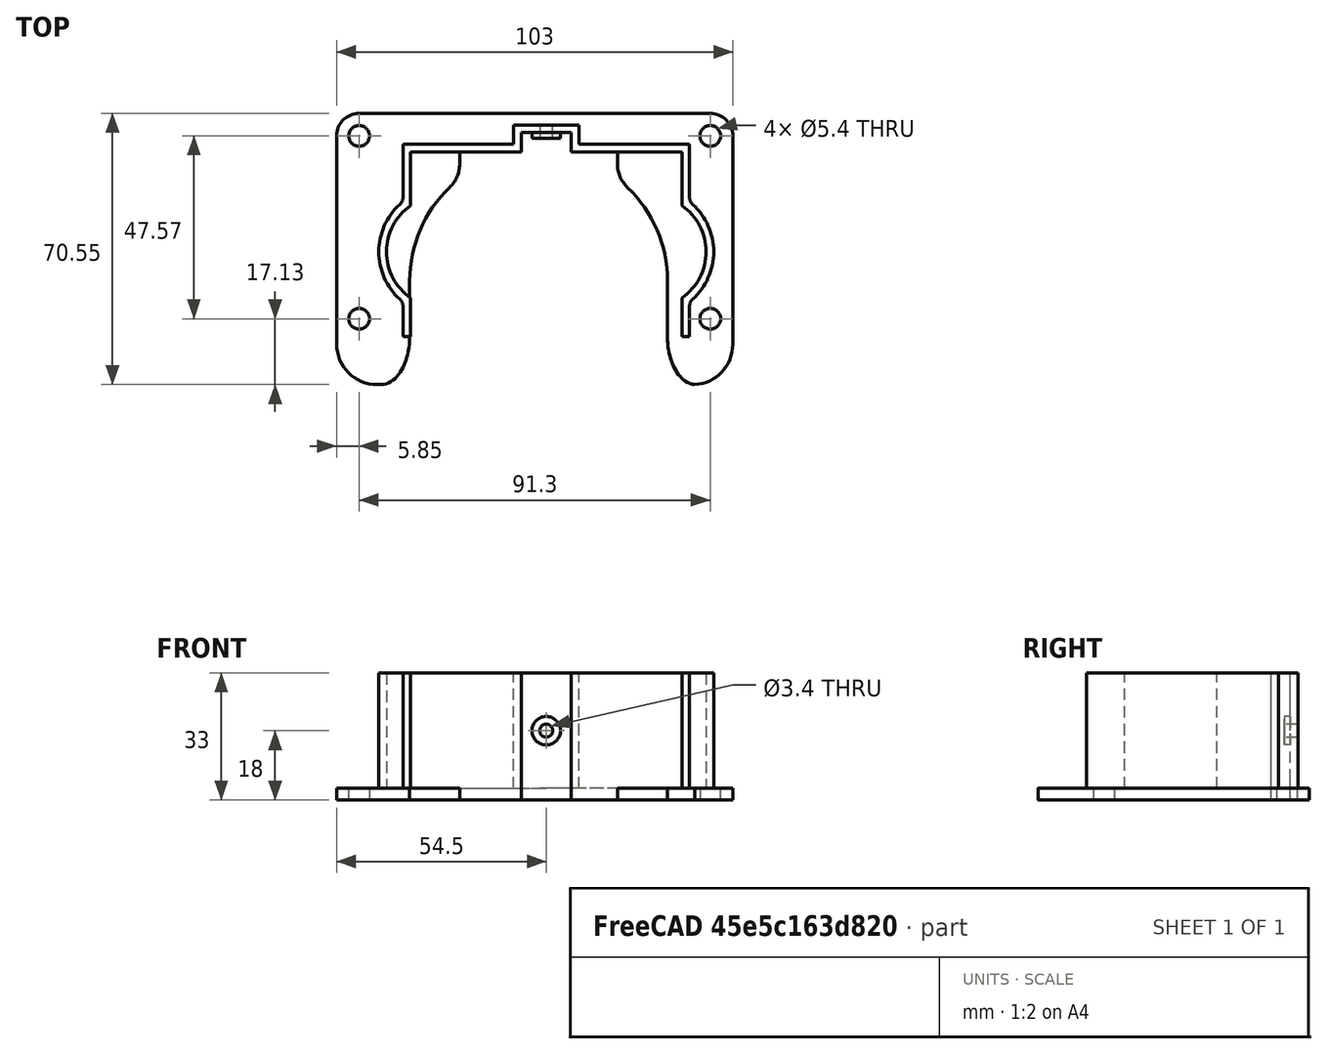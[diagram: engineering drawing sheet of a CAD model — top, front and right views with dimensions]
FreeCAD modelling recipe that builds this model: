
FCSTD DOCUMENT  (FreeCAD 0.19R24366 (Git))
Label: Направляющая датёра
License: All rights reserved
LicenseURL: http://en.wikipedia.org/wiki/All_rights_reserved
objects: Sketcher::SketchObject×6, PartDesign::Pad×3, PartDesign::Pocket×3, PartDesign::Mirrored×3, Mesh::Feature×1, PartDesign::Body×1
note: 22 computed .brp shape members not serialized (recipe doc carries the construction recipe); baked Part::Feature solids carry a one-line shape summary decoded from their .brp

FEATURE [Mesh::Feature] _____________________________________7  label="Направляющая датёра7"
FEATURE [Sketcher::SketchObject] Sketch
  FullyConstrained = true
  MapMode = 5
  Support = -> [XY_Plane]
  sketch-geometry (8):
    g0: Circle CenterX=45.65 CenterY=30.15 CenterZ=0 NormalX=0 NormalY=0 NormalZ=1 AngleXU=0 Radius=2.7
    g1: Circle CenterX=45.65 CenterY=-17.42 CenterZ=0 NormalX=0 NormalY=0 NormalZ=1 AngleXU=0 Radius=2.7
    g2: ArcOfCircle CenterX=45.65 CenterY=30.15 CenterZ=0 NormalX=0 NormalY=0 NormalZ=1 AngleXU=0 Radius=5.85 StartAngle=6.28319 EndAngle=7.85398
    g3: ArcOfCircle CenterX=41 CenterY=-24.05 CenterZ=0 NormalX=0 NormalY=0 NormalZ=1 AngleXU=0 Radius=10.5 StartAngle=4.71239 EndAngle=6.28319
    g4: LineSegment StartX=45.65 StartY=36 StartZ=0 EndX=0 EndY=36 EndZ=0
    g5: LineSegment StartX=0 StartY=36 StartZ=0 EndX=0 EndY=-34.55 EndZ=0
    g6: LineSegment StartX=0 StartY=-34.55 StartZ=0 EndX=41 EndY=-34.55 EndZ=0
    g7: LineSegment StartX=51.5 StartY=-24.05 StartZ=0 EndX=51.5 EndY=30.15 EndZ=0
  constraints (25):
    c: Coincident(g2,g0)
    c: Coincident(g4,g2)
    c: PointOnObject(g4,g-2)
    c: Horizontal(g4)
    c: Coincident(g5,g4)
    c: PointOnObject(g5,g-2)
    c: Coincident(g6,g5)
    c: Coincident(g6,g3)
    c: Coincident(g7,g3)
    c: Coincident(g7,g2)
    c: Vertical(g7)
    c: Horizontal(g6)
    c: Diameter(g0) = 5.4
    c: Vertical(g1,g0)
    c: Equal(g1,g0)
    c: DistanceX(g0) = 45.65
    c: DistanceY(g0) = 30.15
    c: DistanceY(g1) = -17.42
    c: Diameter(g2) = 11.7
    c: Tangent(g2,g4)
    c: Tangent(g2,g7)
    c: Tangent(g3,g7)
    c: Tangent(g6,g3)
    c: Diameter(g3) = 21
    c: DistanceY(g5) = -34.55
FEATURE [Sketcher::SketchObject] Sketch001
  AttachmentOffset = pos=(1,0,0) rot=(0,0,1;0rad)
  FullyConstrained = true
  MapMode = 5
  Placement = pos=(1,0,0) rot=(0,0,1;0rad)
  Support = -> [XY_Plane]
  sketch-geometry (12):
    g0: LineSegment StartX=20.5 StartY=22.8809 StartZ=0 EndX=20.5 EndY=26 EndZ=0
    g1: LineSegment StartX=20.5 StartY=26 StartZ=0 EndX=0 EndY=26 EndZ=0
    g2: ArcOfCircle CenterX=29 CenterY=22.8809 CenterZ=0 NormalX=0 NormalY=0 NormalZ=1 AngleXU=0 Radius=8.5 StartAngle=3.14159 EndAngle=3.95024
    g3: ArcOfCircle CenterX=0 CenterY=-7.5 CenterZ=0 NormalX=0 NormalY=0 NormalZ=1 AngleXU=0 Radius=33.5 StartAngle=8.26042e-09 EndAngle=0.808649
    g4: LineSegment StartX=41 StartY=-34.55 StartZ=0 EndX=0 EndY=-34.55 EndZ=0
    g5: LineSegment StartX=0 StartY=-34.55 StartZ=0 EndX=0 EndY=26 EndZ=0
    g6: LineSegment StartX=33.5 StartY=-7.5 StartZ=0 EndX=33.5 EndY=-22 EndZ=0
    g7: ArcOfEllipse CenterX=41 CenterY=-22 CenterZ=0 NormalX=0 NormalY=0 NormalZ=1 MajorRadius=12.55 MinorRadius=7.5 AngleXU=1.5708 StartAngle=1.5708 EndAngle=3.14159
    g8: LineSegment StartX=41 StartY=-9.45 StartZ=0 EndX=41 EndY=-34.55 EndZ=0
    g9: LineSegment StartX=33.5 StartY=-22 StartZ=0 EndX=48.5 EndY=-22 EndZ=0
    g10: GeomPoint X=41 Y=-11.9376 Z=0
    g11: GeomPoint X=41 Y=-32.0624 Z=0
  constraints (30):
    c: Vertical(g0)
    c: Coincident(g1,g0)
    c: PointOnObject(g1,g-2)
    c: Horizontal(g1)
    c: Coincident(g2,g0)
    c: PointOnObject(g3,g-2)
    c: Coincident(g3,g2)
    c: PointOnObject(g4,g-2)
    c: Horizontal(g4)
    c: Coincident(g5,g4)
    c: Coincident(g5,g1)
    c: DistanceY(g4) = -34.55
    c: Coincident(g6,g3)
    c: Vertical(g6)
    c: Diameter(g3) = 67
    c: DistanceY(g1) = 26
    c: DistanceX(g0) = 20.5
    c: PointOnObject(g1,g3)
    c: Tangent(g3,g2)
    c: Tangent(g2,g0)
    c: Diameter(g2) = 17
    c: Tangent(g6,g3)
    c: InternalAlignment(g8-g11 -> g7) x4
    c: Coincident(g7,g4)
    c: Coincident(g7,g6)
    c: Vertical(g8)
    c: Tangent(g7,g6)
    c: Tangent(g7,g4)
    c: DistanceY(g6) = -22
    c: DistanceX(g4) = 41
FEATURE [Sketcher::SketchObject] Sketch002
  AttachmentOffset = pos=(3,0,3) rot=(0,0,1;0rad)
  FullyConstrained = true
  MapMode = 5
  Placement = pos=(3,0,3) rot=(0,0,1;0rad)
  Support = -> [XY_Plane]
  expr: Constraints[60] = Sketch001.Constraints[14]
  expr: Constraints[62] = Sketch001.Constraints[16]
  expr: Constraints[61] = Sketch001.Constraints[15]
  expr: Constraints[66] = Sketch001.Constraints[20]
  expr: Constraints[57] = Sketch001.Constraints[11]
  expr: Constraints[77] = Sketch001.Constraints[31]
  expr: Constraints[78] = Sketch001.Constraints[32]
  sketch-geometry (31):
    g0: LineSegment StartX=35.25 StartY=-22 StartZ=0 EndX=37.25 EndY=-22 EndZ=0
    g1: LineSegment StartX=35.25 StartY=-22 StartZ=0 EndX=35.25 EndY=-12 EndZ=0
    g2: LineSegment StartX=35.25 StartY=12 StartZ=0 EndX=35.25 EndY=26 EndZ=0
    g3: LineSegment StartX=35.25 StartY=26 StartZ=0 EndX=6.5 EndY=26 EndZ=0
    g4: LineSegment StartX=6.5 StartY=26 StartZ=0 EndX=6.5 EndY=31 EndZ=0
    g5: LineSegment StartX=6.5 StartY=31 StartZ=0 EndX=0 EndY=31 EndZ=0
    g6: LineSegment StartX=37.25 StartY=-22 StartZ=0 EndX=37.25 EndY=-14.1617 EndZ=0
    g7: LineSegment StartX=37.25 StartY=14.1617 StartZ=0 EndX=37.25 EndY=28 EndZ=0
    g8: LineSegment StartX=37.25 StartY=28 StartZ=0 EndX=8.5 EndY=28 EndZ=0
    g9: LineSegment StartX=8.5 StartY=28 StartZ=0 EndX=8.5 EndY=33 EndZ=0
    g10: LineSegment StartX=8.5 StartY=33 StartZ=0 EndX=0 EndY=33 EndZ=0
    g11: ArcOfCircle CenterX=26.9338 CenterY=1.9e-15 CenterZ=0 NormalX=0 NormalY=0 NormalZ=1 AngleXU=0 Radius=14.6 StartAngle=5.31842 EndAngle=7.24796
    g12: ArcOfCircle CenterX=26.9338 CenterY=1.9e-15 CenterZ=0 NormalX=0 NormalY=0 NormalZ=1 AngleXU=0 Radius=16.6 StartAngle=5.44796 EndAngle=7.11842
    g13: ArcOfCircle CenterX=39.75 CenterY=14.1617 CenterZ=0 NormalX=0 NormalY=0 NormalZ=1 AngleXU=0 Radius=2.5 StartAngle=3.14159 EndAngle=3.97682
    g14: ArcOfCircle CenterX=39.75 CenterY=-14.1617 CenterZ=0 NormalX=0 NormalY=0 NormalZ=1 AngleXU=0 Radius=2.5 StartAngle=2.30636 EndAngle=3.14159
    g15: LineSegment StartX=35.25 StartY=26 StartZ=0 EndX=37.25 EndY=26 EndZ=0
    g16: LineSegment StartX=8.5 StartY=28 StartZ=0 EndX=8.5 EndY=26 EndZ=0
    g17: LineSegment StartX=0 StartY=33 StartZ=0 EndX=0 EndY=31 EndZ=0
    g18: LineSegment StartX=20.5 StartY=22.8809 StartZ=0 EndX=20.5 EndY=26 EndZ=0
    g19: LineSegment StartX=20.5 StartY=26 StartZ=0 EndX=0 EndY=26 EndZ=0
    g20: ArcOfCircle CenterX=29 CenterY=22.8809 CenterZ=0 NormalX=0 NormalY=0 NormalZ=1 AngleXU=0 Radius=8.5 StartAngle=3.14159 EndAngle=3.95024
    g21: ArcOfCircle CenterX=0 CenterY=-7.5 CenterZ=0 NormalX=0 NormalY=0 NormalZ=1 AngleXU=0 Radius=33.5 StartAngle=6.28319 EndAngle=7.09183
    g22: LineSegment StartX=41 StartY=-34.55 StartZ=0 EndX=0 EndY=-34.55 EndZ=0
    g23: LineSegment StartX=0 StartY=-34.55 StartZ=0 EndX=0 EndY=26 EndZ=0
    g24: LineSegment StartX=33.5 StartY=-7.5 StartZ=0 EndX=33.5 EndY=-22 EndZ=0
    g25: ArcOfEllipse CenterX=41 CenterY=-22 CenterZ=0 NormalX=0 NormalY=0 NormalZ=1 MajorRadius=12.55 MinorRadius=7.5 AngleXU=1.5708 StartAngle=1.5708 EndAngle=3.14159
    g26: LineSegment StartX=41 StartY=-9.45 StartZ=0 EndX=41 EndY=-34.55 EndZ=0
    g27: LineSegment StartX=33.5 StartY=-22 StartZ=0 EndX=48.5 EndY=-22 EndZ=0
    g28: GeomPoint X=41 Y=-11.9376 Z=0
    g29: GeomPoint X=41 Y=-32.0624 Z=0
    g30: LineSegment StartX=8.5 StartY=28 StartZ=0 EndX=6.5 EndY=28 EndZ=0
  constraints (89):
    c: Horizontal(g0)
    c: Coincident(g1,g0)
    c: Vertical(g1)
    c: Vertical(g2)
    c: Coincident(g3,g2)
    c: Horizontal(g3)
    c: Coincident(g4,g3)
    c: Vertical(g4)
    c: Coincident(g5,g4)
    c: Horizontal(g5)
    c: Coincident(g6,g0)
    c: Vertical(g6)
    c: Vertical(g7)
    c: Coincident(g8,g7)
    c: Horizontal(g8)
    c: Coincident(g9,g8)
    c: Vertical(g9)
    c: Coincident(g10,g9)
    c: PointOnObject(g10,g-2)
    c: Horizontal(g10)
    c: Coincident(g11,g1)
    c: Coincident(g11,g2)
    c: DistanceX(g1) = 35.25
    c: DistanceY(g1) = -12
    c: Diameter(g11) = 29.2
    c: Coincident(g12,g11)
    c: Diameter(g12) = 33.2
    c: Coincident(g13,g12)
    c: Coincident(g13,g7)
    c: Coincident(g14,g6)
    c: Coincident(g14,g12)
    c: Diameter(g14) = 5
    c: Distance(g0) = 2
    c: Coincident(g15,g2)
    c: PointOnObject(g15,g7)
    c: Horizontal(g15)
    c: Equal(g0,g15)
    c: Coincident(g16,g8)
    c: PointOnObject(g16,g3)
    c: Vertical(g16)
    c: Equal(g16,g15)
    c: Equal(g14,g13)
    c: Distance(g4) = 5
    c: Coincident(g17,g10)
    c: Coincident(g17,g5)
    c: Vertical(g17)
    c: Vertical(g18)
    c: Coincident(g19,g18)
    c: PointOnObject(g19,g-2)
    c: Horizontal(g19)
    c: Coincident(g20,g18)
    c: PointOnObject(g21,g-2)
    c: Coincident(g21,g20)
    c: PointOnObject(g22,g-2)
    c: Horizontal(g22)
    c: Coincident(g23,g22)
    c: Coincident(g23,g19)
    c: DistanceY(g22) = -34.55
    c: Coincident(g24,g21)
    c: Vertical(g24)
    c: Diameter(g21) = 67
    c: DistanceY(g19) = 26
    c: DistanceX(g18) = 20.5
    c: PointOnObject(g19,g21)
    c: Tangent(g21,g20)
    c: Tangent(g20,g18)
    c: Diameter(g20) = 17
    c: Tangent(g24,g21)
    c: InternalAlignment(g26-g29 -> g25) x4
    c: Coincident(g25,g22)
    c: Coincident(g25,g24)
    c: Vertical(g26)
    c: Tangent(g25,g24)
    c: Tangent(g25,g22)
    c: DistanceY(g24) = -22
    c: DistanceX(g22) = 41
    c: PointOnObject(g3,g19)
    c: Coincident(g30,g8)
    c: PointOnObject(g30,g4)
    c: Horizontal(g30)
    c: Equal(g16,g30)
    c: Distance(g5) = 6.5
    c: Equal(g0,g17)
    c: Tangent(g13,g7)
    c: Tangent(g12,g13)
    c: Tangent(g12,g14)
    c: Tangent(g14,g6)
    c: Distance(g1) = 10
    c: Symmetric(g1,g2,g-1)
FEATURE [PartDesign::Pad] Pad
  Direction = (1,1,1)
  Length = 3
  Length2 = 100
  Profile = -> Sketch
  Type = 0
FEATURE [PartDesign::Pocket] Pocket
  BaseFeature = -> Pad
  Length = 5
  Length2 = 100
  Profile = -> Sketch001
  Reversed = true
  Type = 0
FEATURE [PartDesign::Pad] Pad001
  BaseFeature = -> Pocket
  Direction = (1,1,1)
  Length = 30
  Length2 = 100
  Profile = -> Sketch002
  Type = 0
FEATURE [Sketcher::SketchObject] Sketch004
  AttachmentOffset = pos=(3,0,0) rot=(0,0,1;0rad)
  FullyConstrained = true
  MapMode = 5
  Placement = pos=(3,0,0) rot=(0,0,1;0rad)
  Support = -> [XY_Plane]
  sketch-geometry (4):
    g0: LineSegment StartX=0 StartY=26 StartZ=0 EndX=6.5 EndY=26 EndZ=0
    g1: LineSegment StartX=6.5 StartY=26 StartZ=0 EndX=6.5 EndY=31 EndZ=0
    g2: LineSegment StartX=6.5 StartY=31 StartZ=0 EndX=0 EndY=31 EndZ=0
    g3: LineSegment StartX=0 StartY=31 StartZ=0 EndX=0 EndY=26 EndZ=0
  constraints (12):
    c: Coincident(g0,g1)
    c: Coincident(g1,g2)
    c: Coincident(g2,g3)
    c: Coincident(g3,g0)
    c: Horizontal(g0)
    c: Horizontal(g2)
    c: Vertical(g1)
    c: Vertical(g3)
    c: PointOnObject(g0,g-2)
    c: DistanceY(g0) = 26
    c: Distance(g3) = 5
    c: Distance(g0) = 6.5
FEATURE [Sketcher::SketchObject] Sketch005
  AttachmentOffset = pos=(3,0,-29.5) rot=(0,0,1;0rad)
  FullyConstrained = true
  MapMode = 5
  Placement = pos=(3,29.5,6.6e-15) rot=(1,0,0;1.5708rad)
  Support = -> [XZ_Plane]
  sketch-geometry (1):
    g0: Circle CenterX=0 CenterY=18 CenterZ=0 NormalX=0 NormalY=0 NormalZ=1 AngleXU=0 Radius=3.7
  constraints (3):
    c: Diameter(g0) = 7.4
    c: DistanceY(g0) = 18
    c: PointOnObject(g0,g-2)
FEATURE [Sketcher::SketchObject] Sketch006
  AttachmentOffset = pos=(3,0,0) rot=(0,0,1;0rad)
  FullyConstrained = true
  MapMode = 5
  Placement = pos=(3,0,0) rot=(1,0,0;1.5708rad)
  Support = -> [XZ_Plane]
  expr: Constraints[1] = Sketch005.Constraints[1]
  sketch-geometry (1):
    g0: Circle CenterX=0 CenterY=18 CenterZ=0 NormalX=0 NormalY=0 NormalZ=1 AngleXU=0 Radius=1.7
  constraints (3):
    c: Diameter(g0) = 3.4
    c: DistanceY(g0) = 18
    c: PointOnObject(g0,g-2)
FEATURE [PartDesign::Pocket] Pocket001
  BaseFeature = -> Pad001
  Length = 5
  Length2 = 100
  Profile = -> Sketch004
  Reversed = true
  Type = 0
FEATURE [PartDesign::Mirrored] Mirrored
  BaseFeature = -> Pocket001
  MirrorPlane = -> Sketch [V_Axis]
  Originals = -> [Pad]
FEATURE [PartDesign::Mirrored] Mirrored001
  BaseFeature = -> Mirrored
  MirrorPlane = -> Sketch001 [V_Axis]
  Originals = -> [Pocket]
FEATURE [PartDesign::Mirrored] Mirrored002
  BaseFeature = -> Mirrored001
  MirrorPlane = -> Sketch002 [V_Axis]
  Originals = -> [Pad001,Pocket001]
FEATURE [PartDesign::Pad] Pad002
  BaseFeature = -> Mirrored002
  Direction = (1,1,1)
  Length = 10
  Length2 = 100
  Profile = -> Sketch005
  Reversed = true
  Type = 1
FEATURE [PartDesign::Pocket] Pocket002
  BaseFeature = -> Pad002
  Length = 5
  Length2 = 100
  Profile = -> Sketch006
  Type = 1
FEATURE [PartDesign::Body] Body
  Group = -> [Sketch,Sketch001,Sketch002,Pad,Pocket,Pad001,Sketch004,Sketch005,Sketch006,Pocket001,Mirrored,Mirrored001,Mirrored002,Pad002,Pocket002]
  Origin = -> Origin
  Tip = -> Pocket002
